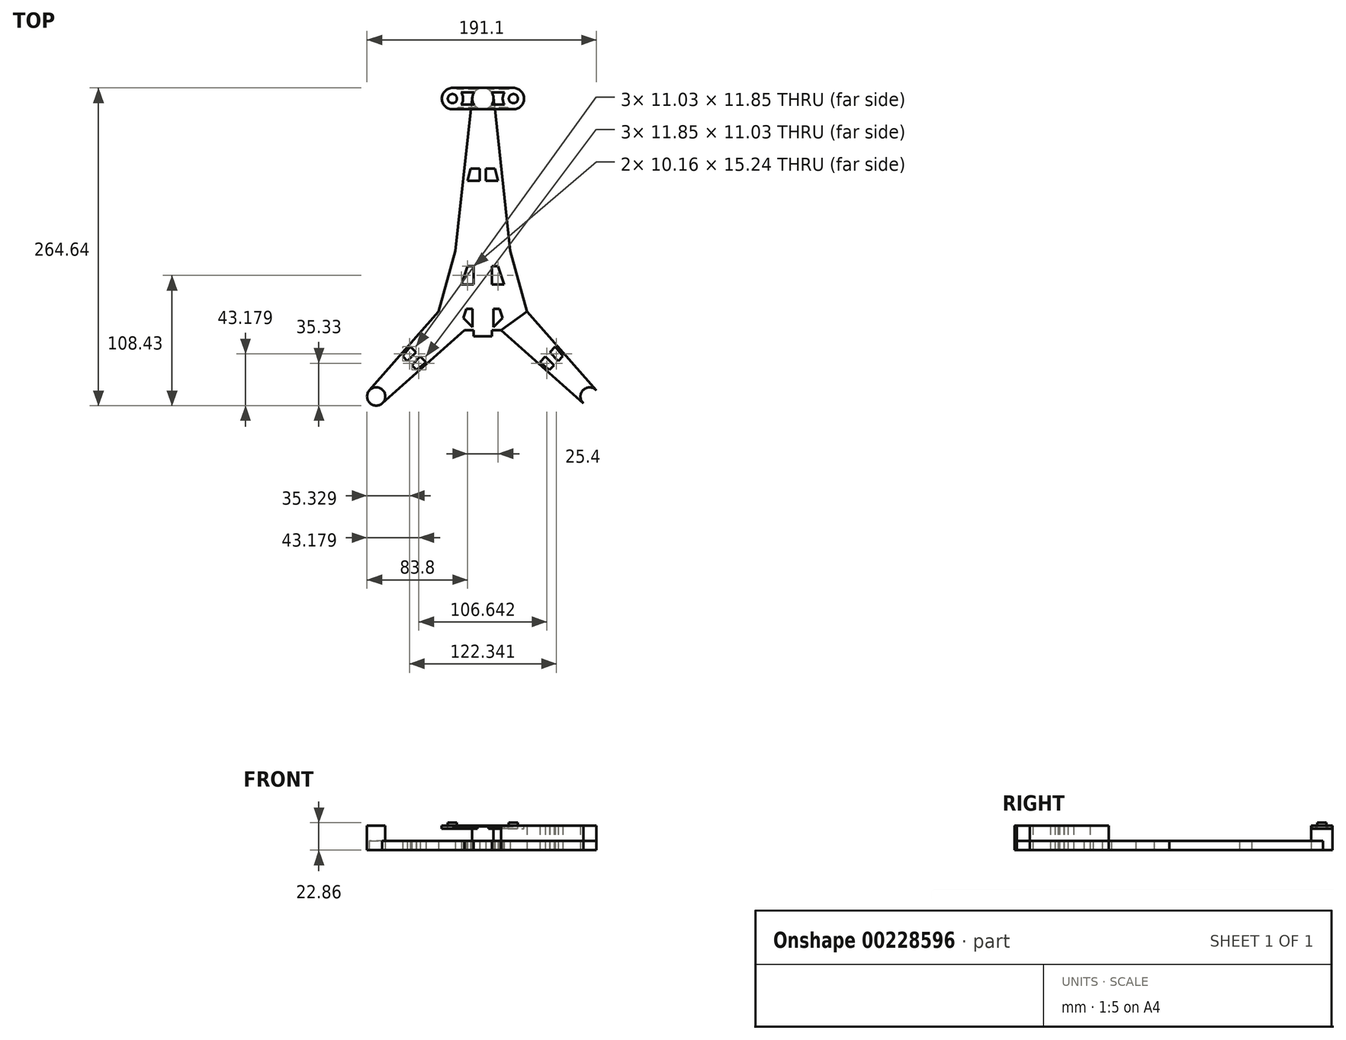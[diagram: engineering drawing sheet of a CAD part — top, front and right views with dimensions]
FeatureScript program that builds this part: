
annotation { "Feature Type Name" : "Feature", "Feature Type Description" : "" }
export const myFeature = defineFeature(function(context is Context, id is Id, definition is map)
    precondition{}
    {
        {
            var Q0;
            Q0=qCreatedBy(makeId("Top.planeOp"),FACE);
            var sketch = newSketch(context, id + "F0", { "sketchPlane" : qUnion([Q0])});
            skLineSegment(sketch, "E0", {"start": v(0, 0) * mm, "end": v(-36.8, -9.86) * mm, "construction": true});
            skLineSegment(sketch, "E1.MirrorCS", {"start": v(0, 0) * mm, "end": v(36.8, -9.86) * mm, "construction": true});
            skLineSegment(sketch, "E2", {"start": v(0, 0) * mm, "end": v(0, 40.64) * mm, "construction": true});
            skPoint(sketch, "E3", {"position": v(-22.86, 40.64) * mm});
            skPoint(sketch, "E4", {"position": v(22.86, 40.64) * mm});
            skLineSegment(sketch, "E5", {"start": v(0, 0) * mm, "end": v(0, -30.48) * mm, "construction": true});
            skPoint(sketch, "E6", {"position": v(0, -25.4) * mm});
            skPoint(sketch, "E7", {"position": v(-15.24, -25.4) * mm});
            skPoint(sketch, "E8", {"position": v(15.24, -25.4) * mm});
            skLineSegment(sketch, "E9", {"start": v(-36.8, -9.86) * mm, "end": v(-15.24, -25.4) * mm});
            skLineSegment(sketch, "E10", {"start": v(-36.8, -9.86) * mm, "end": v(-22.86, 40.64) * mm});
            skLineSegment(sketch, "E11", {"start": v(-22.86, 40.64) * mm, "end": v(0, 40.64) * mm});
            skLineSegment(sketch, "E12", {"start": v(0, 40.64) * mm, "end": v(22.86, 40.64) * mm});
            skLineSegment(sketch, "E13", {"start": v(22.86, 40.64) * mm, "end": v(36.8, -9.86) * mm});
            skLineSegment(sketch, "E14", {"start": v(36.8, -9.86) * mm, "end": v(15.24, -25.4) * mm});
            skLineSegment(sketch, "E15", {"start": v(-15.24, -25.4) * mm, "end": v(0, -25.4) * mm});
            skLineSegment(sketch, "E16", {"start": v(0, -25.4) * mm, "end": v(15.24, -25.4) * mm});
            skLineSegment(sketch, "E17", {"start": v(-7.62, -25.4) * mm, "end": v(-7.62, -30.48) * mm});
            skLineSegment(sketch, "E18.MirrorCS", {"start": v(7.62, -25.4) * mm, "end": v(7.62, -30.48) * mm});
            skLineSegment(sketch, "E19", {"start": v(-7.62, -30.48) * mm, "end": v(7.62, -30.48) * mm});
            skLineSegment(sketch, "E20", {"start": v(-26.02, -17.63) * mm, "end": v(-88.88, -80.5) * mm, "construction": true});
            skLineSegment(sketch, "E21.MirrorCS", {"start": v(26.02, -17.63) * mm, "end": v(88.88, -80.5) * mm, "construction": true});
            skCircle(sketch, "E22", {"center": v(-88.88, -80.5) * mm, "radius": 7.62 * mm});
            skLineSegment(sketch, "E23", {"start": v(-94.6, -75.45) * mm, "end": v(-36.8, -9.86) * mm});
            skLineSegment(sketch, "E24", {"start": v(-83.83, -86.2) * mm, "end": v(-15.24, -25.4) * mm});
            skCircle(sketch, "E25.MirrorC", {"center": v(88.88, -80.5) * mm, "radius": 7.62 * mm});
            skLineSegment(sketch, "E26.MirrorCS", {"start": v(83.83, -86.2) * mm, "end": v(15.24, -25.4) * mm});
            skLineSegment(sketch, "E27.MirrorCS", {"start": v(94.6, -75.45) * mm, "end": v(36.8, -9.86) * mm});
            skLineSegment(sketch, "E28", {"start": v(0, 40.64) * mm, "end": v(0, 167.64) * mm, "construction": true});
            skCircle(sketch, "E29", {"center": v(0, 167.64) * mm, "radius": 8.9 * mm});
            skLineSegment(sketch, "E30", {"start": v(-8.84, 168.6) * mm, "end": v(-22.86, 40.64) * mm});
            skLineSegment(sketch, "E31", {"start": v(8.84, 168.6) * mm, "end": v(22.86, 40.64) * mm});
            skPoint(sketch, "E32", {"position": v(-7.62, 20.32) * mm});
            skPoint(sketch, "E32.positionSnap0", {"position": v(0, 20.32) * mm});
            skLineSegment(sketch, "E33", {"start": v(-7.62, 20.32) * mm, "end": v(-7.62, 27.94) * mm});
            skLineSegment(sketch, "E34", {"start": v(-7.62, 20.32) * mm, "end": v(-7.62, 12.7) * mm});
            skLineSegment(sketch, "E35", {"start": v(-7.62, 27.94) * mm, "end": v(-12.7, 27.94) * mm});
            skLineSegment(sketch, "E36", {"start": v(-7.62, 12.7) * mm, "end": v(-17.78, 12.7) * mm});
            skLineSegment(sketch, "E37", {"start": v(-17.78, 12.7) * mm, "end": v(-12.7, 27.94) * mm});
            skLineSegment(sketch, "E38.MirrorCS", {"start": v(7.62, 12.7) * mm, "end": v(17.78, 12.7) * mm});
            skLineSegment(sketch, "E39.MirrorCS", {"start": v(17.78, 12.7) * mm, "end": v(12.7, 27.94) * mm});
            skLineSegment(sketch, "E40.MirrorCS", {"start": v(7.62, 20.32) * mm, "end": v(7.62, 27.94) * mm});
            skLineSegment(sketch, "E41.MirrorCS", {"start": v(7.62, 20.32) * mm, "end": v(7.62, 12.7) * mm});
            skLineSegment(sketch, "E42.MirrorCS", {"start": v(7.62, 27.94) * mm, "end": v(12.7, 27.94) * mm});
            skPoint(sketch, "E43", {"position": v(-8.71, -15.24) * mm});
            skPoint(sketch, "E43.positionSnap0", {"position": v(0, -15.24) * mm});
            skLineSegment(sketch, "E44", {"start": v(-8.71, -15.24) * mm, "end": v(-8.71, -7.62) * mm});
            skLineSegment(sketch, "E45", {"start": v(-8.71, -15.24) * mm, "end": v(-8.71, -22.86) * mm});
            skLineSegment(sketch, "E46", {"start": v(-8.71, -7.62) * mm, "end": v(-13.8, -7.62) * mm});
            skLineSegment(sketch, "E47", {"start": v(-8.71, -22.86) * mm, "end": v(-16.33, -15.24) * mm});
            skLineSegment(sketch, "E48", {"start": v(-16.33, -15.24) * mm, "end": v(-13.8, -7.62) * mm});
            skLineSegment(sketch, "E49.MirrorCS", {"start": v(8.71, -15.24) * mm, "end": v(8.71, -7.62) * mm});
            skLineSegment(sketch, "E50.MirrorCS", {"start": v(16.33, -15.24) * mm, "end": v(13.8, -7.62) * mm});
            skLineSegment(sketch, "E51.MirrorCS", {"start": v(8.71, -22.86) * mm, "end": v(16.33, -15.24) * mm});
            skLineSegment(sketch, "E52.MirrorCS", {"start": v(8.71, -15.24) * mm, "end": v(8.71, -22.86) * mm});
            skLineSegment(sketch, "E53.MirrorCS", {"start": v(8.71, -7.62) * mm, "end": v(13.8, -7.62) * mm});
            skPoint(sketch, "E54", {"position": v(2.54, 104.14) * mm});
            skPoint(sketch, "E54.positionSnap0", {"position": v(0, 104.14) * mm});
            skLineSegment(sketch, "E55", {"start": v(2.54, 104.14) * mm, "end": v(2.54, 99.06) * mm});
            skLineSegment(sketch, "E56", {"start": v(2.54, 104.14) * mm, "end": v(2.54, 109.22) * mm});
            skLineSegment(sketch, "E57", {"start": v(2.54, 109.22) * mm, "end": v(10.16, 109.22) * mm});
            skLineSegment(sketch, "E58", {"start": v(2.54, 99.06) * mm, "end": v(12.7, 99.06) * mm});
            skLineSegment(sketch, "E59", {"start": v(10.16, 109.22) * mm, "end": v(12.7, 99.06) * mm});
            skLineSegment(sketch, "E60.MirrorCS", {"start": v(-10.16, 109.22) * mm, "end": v(-12.7, 99.06) * mm});
            skLineSegment(sketch, "E61.MirrorCS", {"start": v(-2.54, 99.06) * mm, "end": v(-12.7, 99.06) * mm});
            skLineSegment(sketch, "E62.MirrorCS", {"start": v(-2.54, 109.22) * mm, "end": v(-10.16, 109.22) * mm});
            skLineSegment(sketch, "E63.MirrorCS", {"start": v(-2.54, 104.14) * mm, "end": v(-2.54, 109.22) * mm});
            skLineSegment(sketch, "E64.MirrorCS", {"start": v(-2.54, 104.14) * mm, "end": v(-2.54, 99.06) * mm});
            skLineSegment(sketch, "E65", {"start": v(57.45, -49.06) * mm, "end": v(59.25, -47.27) * mm, "construction": true});
            skLineSegment(sketch, "E66", {"start": v(59.25, -47.27) * mm, "end": v(62.84, -50.86) * mm});
            skLineSegment(sketch, "E67", {"start": v(59.25, -47.27) * mm, "end": v(55.66, -43.67) * mm});
            skLineSegment(sketch, "E68", {"start": v(55.66, -43.67) * mm, "end": v(60.33, -39) * mm});
            skLineSegment(sketch, "E69", {"start": v(62.84, -50.86) * mm, "end": v(66.69, -47.01) * mm});
            skLineSegment(sketch, "E70", {"start": v(66.69, -47.01) * mm, "end": v(60.33, -39) * mm});
            skLineSegment(sketch, "E71.MirrorCS", {"start": v(52.06, -47.27) * mm, "end": v(47.4, -51.94) * mm});
            skLineSegment(sketch, "E72.MirrorCS", {"start": v(55.4, -58.3) * mm, "end": v(47.4, -51.94) * mm});
            skLineSegment(sketch, "E73.MirrorCS", {"start": v(55.66, -50.86) * mm, "end": v(52.06, -47.27) * mm});
            skLineSegment(sketch, "E74.MirrorCS", {"start": v(55.66, -50.86) * mm, "end": v(59.25, -54.45) * mm});
            skLineSegment(sketch, "E75.MirrorCS", {"start": v(59.25, -54.45) * mm, "end": v(55.4, -58.3) * mm});
            skLineSegment(sketch, "E76.MirrorCS", {"start": v(-52.06, -47.27) * mm, "end": v(-47.4, -51.94) * mm});
            skLineSegment(sketch, "E77.MirrorCS", {"start": v(-55.4, -58.3) * mm, "end": v(-47.4, -51.94) * mm});
            skLineSegment(sketch, "E78.MirrorCS", {"start": v(-59.25, -54.45) * mm, "end": v(-55.4, -58.3) * mm});
            skLineSegment(sketch, "E79.MirrorCS", {"start": v(-55.66, -50.86) * mm, "end": v(-59.25, -54.45) * mm});
            skLineSegment(sketch, "E80.MirrorCS", {"start": v(-55.66, -50.86) * mm, "end": v(-52.06, -47.27) * mm});
            skLineSegment(sketch, "E81.MirrorCS", {"start": v(-55.66, -43.67) * mm, "end": v(-60.33, -39) * mm});
            skLineSegment(sketch, "E82.MirrorCS", {"start": v(-66.69, -47.01) * mm, "end": v(-60.33, -39) * mm});
            skLineSegment(sketch, "E83.MirrorCS", {"start": v(-62.84, -50.86) * mm, "end": v(-66.69, -47.01) * mm});
            skLineSegment(sketch, "E84.MirrorCS", {"start": v(-59.25, -47.27) * mm, "end": v(-62.84, -50.86) * mm});
            skLineSegment(sketch, "E85.MirrorCS", {"start": v(-59.25, -47.27) * mm, "end": v(-55.66, -43.67) * mm});
            skSolve(sketch);
        }
        {
            var Q0;
            Q0=makeQuery(id+"F0.imprint","IMPRINT",FACE,{"disambiguationData":[TD([[makeQuery(id+"F0.imprint","IMPRINT",EDGE,{"derivedFrom":sQuery(id+"F0.wireOp",EDGE,"E14")}),1.0]])]});
            var Q1;
            Q1=makeQuery(id+"F0.imprint","IMPRINT",FACE,{"disambiguationData":[TD([[makeQuery(id+"F0.imprint","IMPRINT",EDGE,{"derivedFrom":sQuery(id+"F0.wireOp",EDGE,"E9")}),-1.0]])]});
            var Q2;
            {var subQ5=sQuery(id+"F0.wireOp",EDGE,"E9");Q2=makeQuery(id+"F0.imprint","IMPRINT",FACE,{"disambiguationData":[TD([[makeQuery(id+"F0.imprint","IMPRINT",EDGE,{"derivedFrom":subQ5}),1.0]])]});}
            var Q3;
            {var subQ1=sQuery(id+"F0.wireOp",EDGE,"E17");Q3=makeQuery(id+"F0.imprint","IMPRINT",FACE,{"disambiguationData":[TD([[makeQuery(id+"F0.imprint","IMPRINT",EDGE,{"derivedFrom":subQ1}),1.0]])]});}
            var Q4;
            Q4=makeQuery(id+"F0.imprint","IMPRINT",FACE,{"disambiguationData":[TD([[makeQuery(id+"F0.imprint","IMPRINT",EDGE,{"derivedFrom":sQuery(id+"F0.wireOp",EDGE,"E11")}),1.0]])]});
            extrude(context, id + "F1", {"entities" : qUnion([Q0, Q1, Q2, Q3, Q4]), "depth" : 7.62 * mm});
        }
        {
            var Q0;
            {var subQ0=sQuery(id+"F0.wireOp",EDGE,"E29");var subQ1=makeQuery(id+"F0.imprint","INTERSECT",VERTEX,{"derivedFrom":[subQ0,sQuery(id+"F0.wireOp",EDGE,"E30")]});Q0=makeQuery(id+"F0.imprint","IMPRINT",FACE,{"disambiguationData":[TD([[makeQuery(id+"F0.imprint","IMPRINT",EDGE,{"disambiguationData":[TD([[subQ1,1.0]])],"derivedFrom":subQ0}),1.0]])]});}
            var Q1;
            {var subQ0=sQuery(id+"F0.wireOp",EDGE,"E25.MirrorC");var subQ1=makeQuery(id+"F0.imprint","INTERSECT",VERTEX,{"derivedFrom":[subQ0,sQuery(id+"F0.wireOp",EDGE,"E26.MirrorCS")]});Q1=makeQuery(id+"F0.imprint","IMPRINT",FACE,{"disambiguationData":[TD([[makeQuery(id+"F0.imprint","IMPRINT",EDGE,{"disambiguationData":[TD([[subQ1,1.0]])],"derivedFrom":subQ0}),-1.0]])]});}
            var Q2;
            {var subQ0=sQuery(id+"F0.wireOp",EDGE,"E22");var subQ1=makeQuery(id+"F0.imprint","INTERSECT",VERTEX,{"derivedFrom":[subQ0,sQuery(id+"F0.wireOp",EDGE,"E23")]});Q2=makeQuery(id+"F0.imprint","IMPRINT",FACE,{"disambiguationData":[TD([[makeQuery(id+"F0.imprint","IMPRINT",EDGE,{"disambiguationData":[TD([[subQ1,-1.0]])],"derivedFrom":subQ0}),1.0]])]});}
            extrude(context, id + "F2", {"entities" : qUnion([Q0, Q1, Q2]), "depth" : 20.32 * mm});
        }
        {
            var Q0;
            Q0=makeQuery(id+"F2.opExtrude","CAP_FACE",FACE,{"disambiguationData":[OSD([sQuery(id+"F0.wireOp",EDGE,"E29")])],"isStart":false});
            var sketch = newSketch(context, id + "F3", { "sketchPlane" : qUnion([Q0])});
            skLineSegment(sketch, "E86.bottom", {"start": v(-25.4, 176.53) * mm, "end": v(25.4, 176.53) * mm});
            skLineSegment(sketch, "E86.top", {"start": v(-25.4, 158.75) * mm, "end": v(25.4, 158.75) * mm});
            skLineSegment(sketch, "E86.left", {"start": v(-25.4, 176.53) * mm, "end": v(-25.4, 158.75) * mm});
            skLineSegment(sketch, "E86.right", {"start": v(25.4, 176.53) * mm, "end": v(25.4, 158.75) * mm});
            skPoint(sketch, "E86.middle", {"position": v(0, 167.64) * mm});
            skLineSegment(sketch, "E87.bottom", {"start": v(-25.4, 173.99) * mm, "end": v(25.4, 173.99) * mm});
            skLineSegment(sketch, "E87.top", {"start": v(-25.4, 161.29) * mm, "end": v(25.4, 161.29) * mm});
            skLineSegment(sketch, "E87.left", {"start": v(-25.4, 173.99) * mm, "end": v(-25.4, 161.29) * mm});
            skLineSegment(sketch, "E87.right", {"start": v(25.4, 173.99) * mm, "end": v(25.4, 161.29) * mm});
            skCircle(sketch, "E88", {"center": v(25.4, 167.64) * mm, "radius": 8.9 * mm});
            skCircle(sketch, "E89", {"center": v(-25.4, 167.64) * mm, "radius": 8.9 * mm});
            skCircle(sketch, "E90", {"center": v(-25.4, 167.64) * mm, "radius": 3.81 * mm});
            skCircle(sketch, "E91", {"center": v(25.4, 167.64) * mm, "radius": 3.81 * mm});
            skLineSegment(sketch, "E92.bottom", {"start": v(25.4, 175.26) * mm, "end": v(-25.4, 175.26) * mm});
            skLineSegment(sketch, "E92.top", {"start": v(25.4, 160.02) * mm, "end": v(-25.4, 160.02) * mm});
            skLineSegment(sketch, "E92.left", {"start": v(25.4, 175.26) * mm, "end": v(25.4, 160.02) * mm});
            skLineSegment(sketch, "E92.right", {"start": v(-25.4, 175.26) * mm, "end": v(-25.4, 160.02) * mm});
            skLineSegment(sketch, "E93.bottom", {"start": v(-25.4, 172.72) * mm, "end": v(25.4, 172.72) * mm});
            skLineSegment(sketch, "E93.top", {"start": v(-25.4, 162.56) * mm, "end": v(25.4, 162.56) * mm});
            skLineSegment(sketch, "E93.left", {"start": v(-25.4, 172.72) * mm, "end": v(-25.4, 162.56) * mm});
            skLineSegment(sketch, "E93.right", {"start": v(25.4, 172.72) * mm, "end": v(25.4, 162.56) * mm});
            skSolve(sketch);
        }
        {
            var Q0;
            {var subQ0=sQuery(id+"F3.wireOp",EDGE,"E89");var subQ5=sQuery(id+"F3.wireOp",EDGE,"E92.bottom");var subQ6=makeQuery(id+"F3.imprint","INTERSECT",VERTEX,{"derivedFrom":[subQ0,subQ5]});Q0=makeQuery(id+"F3.imprint","IMPRINT",FACE,{"disambiguationData":[TD([[makeQuery(id+"F3.imprint","IMPRINT",EDGE,{"disambiguationData":[TD([[subQ6,1.0]])],"derivedFrom":subQ5}),-1.0]])]});}
            var Q1;
            {var subQ0=sQuery(id+"F3.wireOp",EDGE,"E89");var subQ1=sQuery(id+"F3.wireOp",EDGE,"E87.bottom");var subQ2=makeQuery(id+"F3.imprint","INTERSECT",VERTEX,{"derivedFrom":[subQ1,subQ0]});Q1=makeQuery(id+"F3.imprint","IMPRINT",FACE,{"disambiguationData":[TD([[makeQuery(id+"F3.imprint","IMPRINT",EDGE,{"disambiguationData":[TD([[subQ2,-1.0]])],"derivedFrom":subQ1}),-1.0]])]});}
            var Q2;
            {var subQ0=sQuery(id+"F3.wireOp",EDGE,"E88");var subQ1=sQuery(id+"F3.wireOp",EDGE,"E87.bottom");var subQ2=makeQuery(id+"F3.imprint","INTERSECT",VERTEX,{"derivedFrom":[subQ1,subQ0]});Q2=makeQuery(id+"F3.imprint","IMPRINT",FACE,{"disambiguationData":[TD([[makeQuery(id+"F3.imprint","IMPRINT",EDGE,{"disambiguationData":[TD([[subQ2,1.0]])],"derivedFrom":subQ1}),-1.0]])]});}
            var Q3;
            {var subQ0=sQuery(id+"F3.wireOp",EDGE,"E88");var subQ5=sQuery(id+"F3.wireOp",EDGE,"E92.bottom");var subQ6=makeQuery(id+"F3.imprint","INTERSECT",VERTEX,{"derivedFrom":[subQ0,subQ5]});Q3=makeQuery(id+"F3.imprint","IMPRINT",FACE,{"disambiguationData":[TD([[makeQuery(id+"F3.imprint","IMPRINT",EDGE,{"disambiguationData":[TD([[subQ6,-1.0]])],"derivedFrom":subQ5}),-1.0]])]});}
            var Q4;
            {var subQ0=sQuery(id+"F3.wireOp",EDGE,"E89");var subQ1=sQuery(id+"F3.wireOp",EDGE,"E87.top");var subQ2=makeQuery(id+"F3.imprint","INTERSECT",VERTEX,{"derivedFrom":[subQ1,subQ0]});Q4=makeQuery(id+"F3.imprint","IMPRINT",FACE,{"disambiguationData":[TD([[makeQuery(id+"F3.imprint","IMPRINT",EDGE,{"disambiguationData":[TD([[subQ2,-1.0]])],"derivedFrom":subQ1}),1.0]])]});}
            var Q5;
            {var subQ0=sQuery(id+"F3.wireOp",EDGE,"E89");var subQ5=sQuery(id+"F3.wireOp",EDGE,"E92.top");var subQ6=makeQuery(id+"F3.imprint","INTERSECT",VERTEX,{"derivedFrom":[subQ0,subQ5]});Q5=makeQuery(id+"F3.imprint","IMPRINT",FACE,{"disambiguationData":[TD([[makeQuery(id+"F3.imprint","IMPRINT",EDGE,{"disambiguationData":[TD([[subQ6,1.0]])],"derivedFrom":subQ5}),1.0]])]});}
            var Q6;
            {var subQ0=sQuery(id+"F3.wireOp",EDGE,"E88");var subQ5=sQuery(id+"F3.wireOp",EDGE,"E92.top");var subQ6=makeQuery(id+"F3.imprint","INTERSECT",VERTEX,{"derivedFrom":[subQ0,subQ5]});Q6=makeQuery(id+"F3.imprint","IMPRINT",FACE,{"disambiguationData":[TD([[makeQuery(id+"F3.imprint","IMPRINT",EDGE,{"disambiguationData":[TD([[subQ6,-1.0]])],"derivedFrom":subQ5}),1.0]])]});}
            var Q7;
            {var subQ0=sQuery(id+"F3.wireOp",EDGE,"E88");var subQ1=sQuery(id+"F3.wireOp",EDGE,"E87.top");var subQ2=makeQuery(id+"F3.imprint","INTERSECT",VERTEX,{"derivedFrom":[subQ1,subQ0]});Q7=makeQuery(id+"F3.imprint","IMPRINT",FACE,{"disambiguationData":[TD([[makeQuery(id+"F3.imprint","IMPRINT",EDGE,{"disambiguationData":[TD([[subQ2,1.0]])],"derivedFrom":subQ1}),1.0]])]});}
            extrude(context, id + "F4", {"entities" : qUnion([Q0, Q1, Q2, Q3, Q4, Q5, Q6, Q7]), "operationType" : NewBodyOperationType.ADD, "oppositeDirection" : true, "depth" : 0.5 * mm});
        }
        {
            var Q0;
            {var subQ0=sQuery(id+"F3.wireOp",EDGE,"E93.left");var subQ1=sQuery(id+"F3.wireOp",EDGE,"E90");var subQ2=makeQuery(id+"F3.imprint","INTERSECT",VERTEX,{"disambiguationData":[OD(0.0)],"derivedFrom":[subQ1,subQ0]});Q0=makeQuery(id+"F3.imprint","IMPRINT",FACE,{"disambiguationData":[TD([[makeQuery(id+"F3.imprint","IMPRINT",EDGE,{"disambiguationData":[TD([[subQ2,-1.0]])],"derivedFrom":subQ1}),-1.0]])]});}
            var Q1;
            {var subQ4=sQuery(id+"F3.wireOp",EDGE,"E89");var subQ6=sQuery(id+"F3.wireOp",EDGE,"E93.bottom");var subQ8=makeQuery(id+"F3.imprint","INTERSECT",VERTEX,{"derivedFrom":[subQ4,subQ6]});Q1=makeQuery(id+"F3.imprint","IMPRINT",FACE,{"disambiguationData":[TD([[makeQuery(id+"F3.imprint","IMPRINT",EDGE,{"disambiguationData":[TD([[subQ8,1.0]])],"derivedFrom":subQ4}),1.0]])]});}
            var Q2;
            {var subQ0=sQuery(id+"F3.wireOp",EDGE,"E92.right");var subQ1=sQuery(id+"F3.wireOp",EDGE,"E87.bottom");var subQ2=makeQuery(id+"F3.imprint","INTERSECT",VERTEX,{"derivedFrom":[subQ1,subQ0]});Q2=makeQuery(id+"F3.imprint","IMPRINT",FACE,{"disambiguationData":[TD([[makeQuery(id+"F3.imprint","IMPRINT",EDGE,{"disambiguationData":[TD([[subQ2,-1.0]])],"derivedFrom":subQ1}),-1.0]])]});}
            var Q3;
            {var subQ0=sQuery(id+"F3.wireOp",EDGE,"E92.right");var subQ1=sQuery(id+"F3.wireOp",EDGE,"E87.bottom");var subQ2=makeQuery(id+"F3.imprint","INTERSECT",VERTEX,{"derivedFrom":[subQ1,subQ0]});Q3=makeQuery(id+"F3.imprint","IMPRINT",FACE,{"disambiguationData":[TD([[makeQuery(id+"F3.imprint","IMPRINT",EDGE,{"disambiguationData":[TD([[subQ2,-1.0]])],"derivedFrom":subQ1}),1.0]])]});}
            var Q4;
            {var subQ0=sQuery(id+"F3.wireOp",EDGE,"E89");var subQ3=sQuery(id+"F3.wireOp",EDGE,"E92.bottom");var subQ5=makeQuery(id+"F3.imprint","INTERSECT",VERTEX,{"derivedFrom":[subQ0,subQ3]});Q4=makeQuery(id+"F3.imprint","IMPRINT",FACE,{"disambiguationData":[TD([[makeQuery(id+"F3.imprint","IMPRINT",EDGE,{"disambiguationData":[TD([[subQ5,-1.0]])],"derivedFrom":subQ0}),1.0]])]});}
            var Q5;
            {var subQ0=sQuery(id+"F3.wireOp",EDGE,"E92.right");var subQ1=sQuery(id+"F3.wireOp",EDGE,"E87.top");var subQ2=makeQuery(id+"F3.imprint","INTERSECT",VERTEX,{"derivedFrom":[subQ1,subQ0]});Q5=makeQuery(id+"F3.imprint","IMPRINT",FACE,{"disambiguationData":[TD([[makeQuery(id+"F3.imprint","IMPRINT",EDGE,{"disambiguationData":[TD([[subQ2,-1.0]])],"derivedFrom":subQ1}),1.0]])]});}
            var Q6;
            {var subQ0=sQuery(id+"F3.wireOp",EDGE,"E92.right");var subQ1=sQuery(id+"F3.wireOp",EDGE,"E87.top");var subQ2=makeQuery(id+"F3.imprint","INTERSECT",VERTEX,{"derivedFrom":[subQ1,subQ0]});Q6=makeQuery(id+"F3.imprint","IMPRINT",FACE,{"disambiguationData":[TD([[makeQuery(id+"F3.imprint","IMPRINT",EDGE,{"disambiguationData":[TD([[subQ2,-1.0]])],"derivedFrom":subQ1}),-1.0]])]});}
            var Q7;
            {var subQ0=sQuery(id+"F3.wireOp",EDGE,"E89");var subQ3=sQuery(id+"F3.wireOp",EDGE,"E92.top");var subQ5=makeQuery(id+"F3.imprint","INTERSECT",VERTEX,{"derivedFrom":[subQ0,subQ3]});Q7=makeQuery(id+"F3.imprint","IMPRINT",FACE,{"disambiguationData":[TD([[makeQuery(id+"F3.imprint","IMPRINT",EDGE,{"disambiguationData":[TD([[subQ5,1.0]])],"derivedFrom":subQ0}),1.0]])]});}
            var Q8;
            {var subQ4=sQuery(id+"F3.wireOp",EDGE,"E88");var subQ6=sQuery(id+"F3.wireOp",EDGE,"E93.bottom");var subQ8=makeQuery(id+"F3.imprint","INTERSECT",VERTEX,{"derivedFrom":[subQ4,subQ6]});Q8=makeQuery(id+"F3.imprint","IMPRINT",FACE,{"disambiguationData":[TD([[makeQuery(id+"F3.imprint","IMPRINT",EDGE,{"disambiguationData":[TD([[subQ8,-1.0]])],"derivedFrom":subQ4}),1.0]])]});}
            var Q9;
            {var subQ9=sQuery(id+"F3.wireOp",EDGE,"E93.right");var subQ10=sQuery(id+"F3.wireOp",EDGE,"E91");var subQ11=makeQuery(id+"F3.imprint","INTERSECT",VERTEX,{"disambiguationData":[OD(0.0)],"derivedFrom":[subQ10,subQ9]});Q9=makeQuery(id+"F3.imprint","IMPRINT",FACE,{"disambiguationData":[TD([[makeQuery(id+"F3.imprint","IMPRINT",EDGE,{"disambiguationData":[TD([[subQ11,1.0]])],"derivedFrom":subQ10}),-1.0]])]});}
            var Q10;
            {var subQ0=sQuery(id+"F3.wireOp",EDGE,"E92.left");var subQ1=sQuery(id+"F3.wireOp",EDGE,"E87.bottom");var subQ2=makeQuery(id+"F3.imprint","INTERSECT",VERTEX,{"derivedFrom":[subQ1,subQ0]});Q10=makeQuery(id+"F3.imprint","IMPRINT",FACE,{"disambiguationData":[TD([[makeQuery(id+"F3.imprint","IMPRINT",EDGE,{"disambiguationData":[TD([[subQ2,1.0]])],"derivedFrom":subQ1}),-1.0]])]});}
            var Q11;
            {var subQ0=sQuery(id+"F3.wireOp",EDGE,"E92.left");var subQ1=sQuery(id+"F3.wireOp",EDGE,"E87.bottom");var subQ2=makeQuery(id+"F3.imprint","INTERSECT",VERTEX,{"derivedFrom":[subQ1,subQ0]});Q11=makeQuery(id+"F3.imprint","IMPRINT",FACE,{"disambiguationData":[TD([[makeQuery(id+"F3.imprint","IMPRINT",EDGE,{"disambiguationData":[TD([[subQ2,1.0]])],"derivedFrom":subQ1}),1.0]])]});}
            var Q12;
            {var subQ0=sQuery(id+"F3.wireOp",EDGE,"E88");var subQ3=sQuery(id+"F3.wireOp",EDGE,"E92.bottom");var subQ5=makeQuery(id+"F3.imprint","INTERSECT",VERTEX,{"derivedFrom":[subQ0,subQ3]});Q12=makeQuery(id+"F3.imprint","IMPRINT",FACE,{"disambiguationData":[TD([[makeQuery(id+"F3.imprint","IMPRINT",EDGE,{"disambiguationData":[TD([[subQ5,1.0]])],"derivedFrom":subQ0}),1.0]])]});}
            var Q13;
            {var subQ0=sQuery(id+"F3.wireOp",EDGE,"E92.left");var subQ1=sQuery(id+"F3.wireOp",EDGE,"E87.top");var subQ2=makeQuery(id+"F3.imprint","INTERSECT",VERTEX,{"derivedFrom":[subQ1,subQ0]});Q13=makeQuery(id+"F3.imprint","IMPRINT",FACE,{"disambiguationData":[TD([[makeQuery(id+"F3.imprint","IMPRINT",EDGE,{"disambiguationData":[TD([[subQ2,1.0]])],"derivedFrom":subQ1}),1.0]])]});}
            var Q14;
            {var subQ0=sQuery(id+"F3.wireOp",EDGE,"E92.left");var subQ1=sQuery(id+"F3.wireOp",EDGE,"E87.top");var subQ2=makeQuery(id+"F3.imprint","INTERSECT",VERTEX,{"derivedFrom":[subQ1,subQ0]});Q14=makeQuery(id+"F3.imprint","IMPRINT",FACE,{"disambiguationData":[TD([[makeQuery(id+"F3.imprint","IMPRINT",EDGE,{"disambiguationData":[TD([[subQ2,1.0]])],"derivedFrom":subQ1}),-1.0]])]});}
            var Q15;
            {var subQ0=sQuery(id+"F3.wireOp",EDGE,"E88");var subQ3=sQuery(id+"F3.wireOp",EDGE,"E92.top");var subQ5=makeQuery(id+"F3.imprint","INTERSECT",VERTEX,{"derivedFrom":[subQ0,subQ3]});Q15=makeQuery(id+"F3.imprint","IMPRINT",FACE,{"disambiguationData":[TD([[makeQuery(id+"F3.imprint","IMPRINT",EDGE,{"disambiguationData":[TD([[subQ5,-1.0]])],"derivedFrom":subQ0}),1.0]])]});}
            extrude(context, id + "F5", {"entities" : qUnion([Q0, Q1, Q2, Q3, Q4, Q5, Q6, Q7, Q8, Q9, Q10, Q11, Q12, Q13, Q14, Q15]), "operationType" : NewBodyOperationType.ADD, "oppositeDirection" : true, "depth" : 2.3 * mm});
        }
        {
            var Q0;
            {var subQ0=sQuery(id+"F3.wireOp",EDGE,"E93.right");var subQ1=sQuery(id+"F3.wireOp",EDGE,"E91");var subQ2=makeQuery(id+"F3.imprint","INTERSECT",VERTEX,{"disambiguationData":[OD(0.0)],"derivedFrom":[subQ1,subQ0]});Q0=makeQuery(id+"F3.imprint","IMPRINT",FACE,{"disambiguationData":[TD([[makeQuery(id+"F3.imprint","IMPRINT",EDGE,{"disambiguationData":[TD([[subQ2,1.0]])],"derivedFrom":subQ1}),1.0]])]});}
            var Q1;
            {var subQ0=sQuery(id+"F3.wireOp",EDGE,"E93.right");var subQ1=sQuery(id+"F3.wireOp",EDGE,"E91");var subQ2=makeQuery(id+"F3.imprint","INTERSECT",VERTEX,{"disambiguationData":[OD(0.0)],"derivedFrom":[subQ1,subQ0]});Q1=makeQuery(id+"F3.imprint","IMPRINT",FACE,{"disambiguationData":[TD([[makeQuery(id+"F3.imprint","IMPRINT",EDGE,{"disambiguationData":[TD([[subQ2,-1.0]])],"derivedFrom":subQ1}),1.0]])]});}
            var Q2;
            {var subQ0=sQuery(id+"F3.wireOp",EDGE,"E93.left");var subQ1=sQuery(id+"F3.wireOp",EDGE,"E90");var subQ2=makeQuery(id+"F3.imprint","INTERSECT",VERTEX,{"disambiguationData":[OD(0.0)],"derivedFrom":[subQ1,subQ0]});Q2=makeQuery(id+"F3.imprint","IMPRINT",FACE,{"disambiguationData":[TD([[makeQuery(id+"F3.imprint","IMPRINT",EDGE,{"disambiguationData":[TD([[subQ2,1.0]])],"derivedFrom":subQ1}),1.0]])]});}
            var Q3;
            {var subQ0=sQuery(id+"F3.wireOp",EDGE,"E93.left");var subQ1=sQuery(id+"F3.wireOp",EDGE,"E90");var subQ2=makeQuery(id+"F3.imprint","INTERSECT",VERTEX,{"disambiguationData":[OD(0.0)],"derivedFrom":[subQ1,subQ0]});Q3=makeQuery(id+"F3.imprint","IMPRINT",FACE,{"disambiguationData":[TD([[makeQuery(id+"F3.imprint","IMPRINT",EDGE,{"disambiguationData":[TD([[subQ2,-1.0]])],"derivedFrom":subQ1}),1.0]])]});}
            extrude(context, id + "F6", {"entities" : qUnion([Q0, Q1, Q2, Q3]), "depth" : 2.54 * mm});
        }
    });
